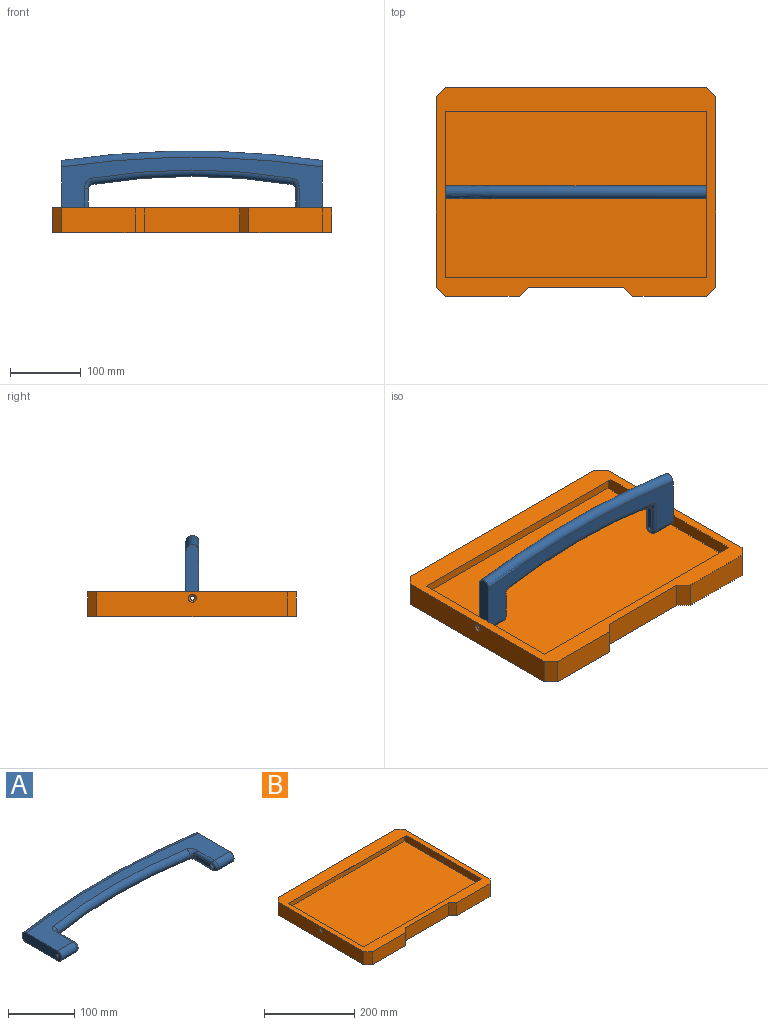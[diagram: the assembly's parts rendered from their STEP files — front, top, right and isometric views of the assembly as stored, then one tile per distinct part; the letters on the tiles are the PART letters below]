
ASSEMBLY  parts=2 mates=1
PART A: 25 faces, bbox 376.5x112.9x18.9 mm
  f0: plane 369.88x81.23mm, normal (0,0,1), area 10488.3mm2, adj f1,f5,f6,f7,f8,f14,f17,f19
  f1: plane 85.55x18.55mm, normal (-1,0,0), area 1433.7mm2, adj f0,f4,f6,f7,f24
  f2: plane 39.93x8mm, normal (1,0,0), area 286.2mm2, adj f9,f11,f12,f14,f24
  f3: plane 39.93x8mm, normal (-1,0,0), area 286.2mm2, adj f10,f18,f20,f22,f23
  f4: plane 369.88x81.23mm, normal (0,0,-1), area 10487.5mm2, adj f1,f5,f6,f7,f8,f11,f13,f15
  f5: plane 85.55x18.55mm, normal (1,0,0), area 1433.7mm2, adj f0,f4,f7,f8,f23
  f6: cylinder r=9mm len=33mm, axis (1,0,0), area 933.1mm2, adj f0,f1,f4,f12
  f7: torus R=1272mm, axis (0,0,1), area 10480.1mm2, adj f0,f1,f4,f5
  f8: cylinder r=9mm len=33mm, axis (1,0,0), area 933.1mm2, adj f0,f4,f5,f20
  f9: cylinder r=6mm len=8mm, axis (0,0,-1), area 33.7mm2, adj f2,f13,f17
  f10: cylinder r=6mm len=8mm, axis (0,0,-1), area 33.7mm2, adj f3,f15,f21
  f11: cylinder r=5mm len=35.93mm, axis (0,1,0), area 282.2mm2, adj f2,f4,f12,f13
  f12: torus R=4mm, axis (-1,0,0), area 177.2mm2, adj f2,f6,f11,f14
  f13: bspline ~14.8x10.04mm, area 134.5mm2, adj f4,f9,f11,f16
  f14: cylinder r=5mm len=35.93mm, axis (0,-1,0), area 282.2mm2, adj f0,f2,f12,f17
  f15: bspline ~14.8x10.04mm, area 134.5mm2, adj f4,f10,f16,f18
  f16: torus R=872mm, axis (0,0,1), area 4033.7mm2, adj f4,f13,f15,f19
  f17: bspline ~14.8x10.04mm, area 134.5mm2, adj f0,f9,f14,f19
  f18: cylinder r=5mm len=35.93mm, axis (0,-1,0), area 282.2mm2, adj f3,f4,f15,f20
  f19: torus R=872mm, axis (0,0,1), area 4033.7mm2, adj f0,f16,f17,f21
  f20: torus R=4mm, axis (-1,0,0), area 177.2mm2, adj f3,f8,f18,f22
  f21: bspline ~14.8x10.04mm, area 134.5mm2, adj f0,f10,f19,f22
  f22: cylinder r=5mm len=35.93mm, axis (0,1,0), area 282.2mm2, adj f0,f3,f20,f21
  f23: cylinder r=2.9mm len=38mm, axis (1,0,0), area 692.4mm2, adj f3,f5
  f24: cylinder r=2.9mm len=38mm, axis (1,0,0), area 692.4mm2, adj f1,f2
PART B: 29 faces, bbox 395x295x35 mm
  f0: plane 395x295mm, normal (0,0,1), area 27179mm2, adj f2,f3,f4,f5,f6,f7,f8,f13
  f1: plane 395x295mm, normal (0,0,-1), area 19799mm2, adj f2,f3,f4,f5,f6,f7,f8,f9
  f2: plane 135x35mm, normal (0,-1,0), area 4725mm2, adj f0,f1,f8,f24
  f3: plane 369x35mm, normal (0,1,0), area 12915mm2, adj f0,f1,f4,f20
  f4: plane 35x13mm, normal (-0.71,0.71,0), area 643.5mm2, adj f0,f1,f3,f5
  f5: plane 269x35mm, normal (-1,0,0), area 9316.5mm2, adj f0,f1,f4,f6,f19
  f6: plane 35x13mm, normal (-0.71,-0.71,0), area 643.5mm2, adj f0,f1,f5,f7
  f7: plane 104x35mm, normal (0,-1,0), area 3640mm2, adj f0,f1,f6,f8
  f8: plane 35x13mm, normal (0.71,-0.71,0), area 643.5mm2, adj f0,f1,f2,f7
  f9: plane 256x15mm, normal (1,0,0), area 3840mm2, adj f1,f10,f11,f12
  f10: plane 369x15mm, normal (0,1,0), area 5535mm2, adj f1,f9,f12,f25
  f11: plane 369x15mm, normal (0,-1,0), area 5535mm2, adj f1,f9,f12,f25
  f12: plane 369x256mm, normal (0,0,-1), area 94464mm2, adj f9,f10,f11,f25
  f13: plane 242x18mm, normal (1,0,0), area 4311.6mm2, adj f0,f14,f15,f16,f17,f18
  f14: plane 369x12mm, normal (0,-1,0), area 4428mm2, adj f13,f15,f16,f26
  f15: plane 369x6mm, normal (0,-0.71,-0.71), area 3131.1mm2, adj f0,f13,f14,f26
  f16: plane 369x242mm, normal (0,0,1), area 89298mm2, adj f13,f14,f17,f26
  f17: plane 369x18mm, normal (0,1,0), area 6642mm2, adj f0,f13,f16,f26
  f18: cylinder r=2.9mm len=10.3mm, axis (-1,0,0), area 187.7mm2, adj f13,f19
  f19: cone r=2.9mm half-angle=45deg, axis (-1,0,0), area 102mm2, adj f5,f18
  f20: plane 35x13mm, normal (0.71,0.71,0), area 643.5mm2, adj f0,f1,f3,f21
  f21: plane 269x35mm, normal (1,0,0), area 9316.5mm2, adj f0,f1,f20,f22,f28
  f22: plane 35x13mm, normal (0.71,-0.71,0), area 643.5mm2, adj f0,f1,f21,f23
  f23: plane 104x35mm, normal (0,-1,0), area 3640mm2, adj f0,f1,f22,f24
  f24: plane 35x13mm, normal (-0.71,-0.71,0), area 643.5mm2, adj f0,f1,f2,f23
  f25: plane 256x15mm, normal (-1,0,0), area 3840mm2, adj f1,f10,f11,f12
  f26: plane 242x18mm, normal (-1,0,0), area 4311.6mm2, adj f0,f14,f15,f16,f17,f27
  f27: cylinder r=2.9mm len=10.3mm, axis (1,0,0), area 187.7mm2, adj f26,f28
  f28: cone r=2.9mm half-angle=45deg, axis (1,0,0), area 102mm2, adj f21,f27
PLACE A rot(axis=(0,-0.71,-0.71),180deg) t=(0,-33,33)mm
PLACE B at identity fixed
MATE revolute A.f6 <-> B.f18  axis (-1,0,0) through (-184.5,-7,26)mm
